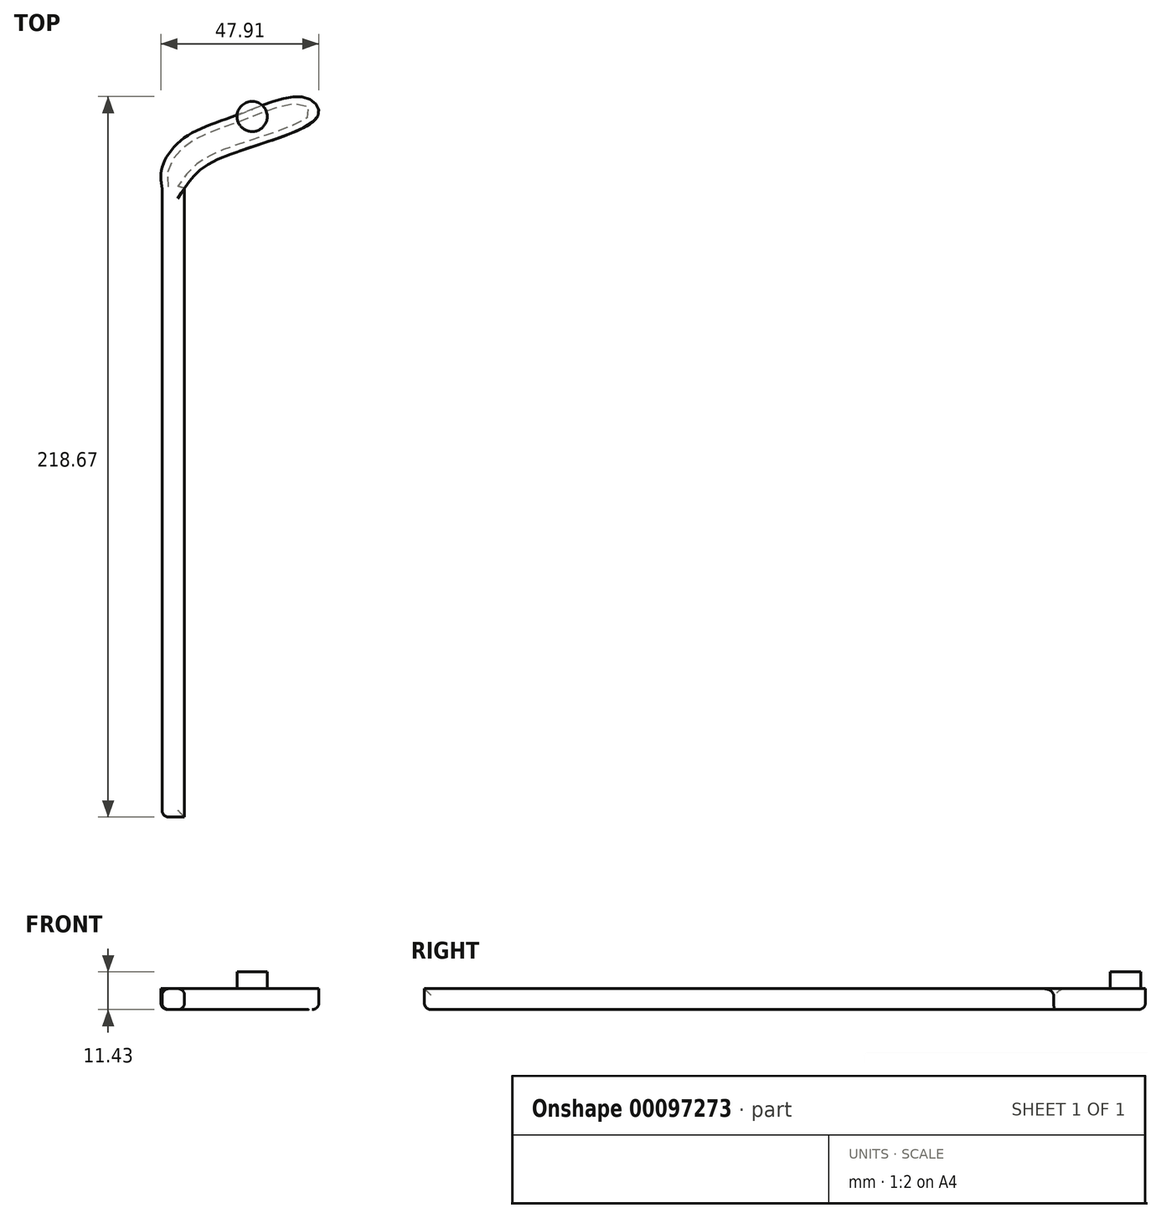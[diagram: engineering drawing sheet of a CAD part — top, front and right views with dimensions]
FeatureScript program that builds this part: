
annotation { "Feature Type Name" : "Feature", "Feature Type Description" : "" }
export const myFeature = defineFeature(function(context is Context, id is Id, definition is map)
    precondition{}
    {
        {
            var Q0;
            Q0=qCreatedBy(makeId("Top.planeOp"),FACE);
            var sketch = newSketch(context, id + "F0", { "sketchPlane" : qUnion([Q0])});
            skLineSegment(sketch, "E0.bottom", {"start": v(-18.72, 95.23) * mm, "end": v(-11.92, 95.23) * mm});
            skLineSegment(sketch, "E0.top", {"start": v(-18.72, -95.62) * mm, "end": v(-11.92, -95.62) * mm});
            skLineSegment(sketch, "E0.left", {"start": v(-18.72, 95.23) * mm, "end": v(-18.72, -95.62) * mm});
            skLineSegment(sketch, "E0.right", {"start": v(-11.92, 95.23) * mm, "end": v(-11.92, -95.62) * mm});
            skFitSpline(sketch, "E1", {"points": [v(-18.72, 95.23) * mm, v(-18.72, 101.6) * mm, v(-12.01, 110.52) * mm, v(5.67, 118.07) * mm, v(24.84, 122.7) * mm, v(28.45, 117) * mm, v(-2.58, 103.66) * mm, v(-11.92, 95.23) * mm], "startDerivative": vector(-9.74, 64.86) * mm, "endDerivative": vector(-42.36, -64.86) * mm});
            skSolve(sketch);
        }
        {
            var Q0;
            Q0=makeQuery(id+"F0.imprint","IMPRINT",FACE,{"disambiguationData":[TD([[makeQuery(id+"F0.imprint","IMPRINT",EDGE,{"derivedFrom":sQuery(id+"F0.wireOp",EDGE,"E0.bottom")}),1.0]])]});
            var Q1;
            Q1=makeQuery(id+"F0.imprint","IMPRINT",FACE,{"disambiguationData":[TD([[makeQuery(id+"F0.imprint","IMPRINT",EDGE,{"derivedFrom":sQuery(id+"F0.wireOp",EDGE,"E0.bottom")}),-1.0]])]});
            extrude(context, id + "F1", {"entities" : qUnion([Q0, Q1]), "depth" : 6.35 * mm});
        }
        {
            var Q0;
            Q0=makeQuery(id+"F1.opExtrude","CAP_EDGE",EDGE,{"disambiguationData":[OSD([sQuery(id+"F0.wireOp",EDGE,"E0.right")])],"isStart":true});
            var Q1;
            Q1=makeQuery(id+"F1.opExtrude","CAP_FACE",FACE,{"disambiguationData":[OSD([sQuery(id+"F0.wireOp",EDGE,"E0.top"),sQuery(id+"F0.wireOp",EDGE,"E0.left"),sQuery(id+"F0.wireOp",EDGE,"E0.right"),sQuery(id+"F0.wireOp",EDGE,"E1")])],"isStart":true});
            var Q2;
            Q2=makeQuery(id+"F1.opExtrude","SWEPT_FACE",FACE,{"disambiguationData":[OSD([sQuery(id+"F0.wireOp",EDGE,"E0.left")])]});
            var Q3;
            Q3=makeQuery(id+"F1.opExtrude","CAP_EDGE",EDGE,{"disambiguationData":[OSD([sQuery(id+"F0.wireOp",EDGE,"E0.left")])],"isStart":true});
            var Q4;
            Q4=makeQuery(id+"F1.opExtrude","CAP_EDGE",EDGE,{"disambiguationData":[OSD([sQuery(id+"F0.wireOp",EDGE,"E0.right")])],"isStart":false});
            fillet(context, id + "F2", {"entities" : qUnion([Q0, Q1, Q2, Q3, Q4]), "radius" : 2.03 * mm, "tangentPropagation" : true, "allowEdgeOverflow" : false});
        }
        {
            var Q0;
            Q0=makeQuery(id+"F1.opExtrude","CAP_FACE",FACE,{"disambiguationData":[OSD([sQuery(id+"F0.wireOp",EDGE,"E0.top"),sQuery(id+"F0.wireOp",EDGE,"E0.left"),sQuery(id+"F0.wireOp",EDGE,"E0.right"),sQuery(id+"F0.wireOp",EDGE,"E1")])],"isStart":false});
            var sketch = newSketch(context, id + "F3", { "sketchPlane" : qUnion([Q0])});
            skCircle(sketch, "E2", {"center": v(8.6, 117.02) * mm, "radius": 4.58 * mm});
            skSolve(sketch);
        }
        {
            var Q0;
            {var subQ0=sQuery(id+"F3.wireOp",EDGE,"E2");var subQ1=sQuery(id+"F0.wireOp",EDGE,"E1");var subQ2=makeQuery(id+"F2.opFillet","BLEND_EDGE",EDGE,{"blendedFrom":[makeQuery(id+"F1.opExtrude","CAP_EDGE",EDGE,{"disambiguationData":[OSD([subQ1])],"isStart":false}),makeQuery(id+"F1.opExtrude","CAP_FACE",FACE,{"disambiguationData":[OSD([sQuery(id+"F0.wireOp",EDGE,"E0.top"),sQuery(id+"F0.wireOp",EDGE,"E0.left"),sQuery(id+"F0.wireOp",EDGE,"E0.right"),subQ1])],"isStart":false})],"blendedInto":[makeQuery(id+"F1.opExtrude","CAP_FACE",FACE,{"disambiguationData":[OSD([sQuery(id+"F0.wireOp",EDGE,"E0.top"),sQuery(id+"F0.wireOp",EDGE,"E0.left"),sQuery(id+"F0.wireOp",EDGE,"E0.right"),subQ1])],"isStart":false})]});var subQ3=makeQuery(id+"F3.imprint","INTERSECT",VERTEX,{"disambiguationData":[OD(0.0)],"derivedFrom":[subQ2,subQ0]});Q0=makeQuery(id+"F3.imprint","IMPRINT",FACE,{"disambiguationData":[TD([[makeQuery(id+"F3.imprint","IMPRINT",EDGE,{"disambiguationData":[TD([[subQ3,1.0]])],"derivedFrom":subQ0}),1.0]])]});}
            var Q1;
            {var subQ0=sQuery(id+"F3.wireOp",EDGE,"E2");var subQ1=sQuery(id+"F0.wireOp",EDGE,"E1");var subQ2=makeQuery(id+"F2.opFillet","BLEND_EDGE",EDGE,{"blendedFrom":[makeQuery(id+"F1.opExtrude","CAP_EDGE",EDGE,{"disambiguationData":[OSD([subQ1])],"isStart":false}),makeQuery(id+"F1.opExtrude","CAP_FACE",FACE,{"disambiguationData":[OSD([sQuery(id+"F0.wireOp",EDGE,"E0.top"),sQuery(id+"F0.wireOp",EDGE,"E0.left"),sQuery(id+"F0.wireOp",EDGE,"E0.right"),subQ1])],"isStart":false})],"blendedInto":[makeQuery(id+"F1.opExtrude","CAP_FACE",FACE,{"disambiguationData":[OSD([sQuery(id+"F0.wireOp",EDGE,"E0.top"),sQuery(id+"F0.wireOp",EDGE,"E0.left"),sQuery(id+"F0.wireOp",EDGE,"E0.right"),subQ1])],"isStart":false})]});var subQ3=makeQuery(id+"F3.imprint","INTERSECT",VERTEX,{"disambiguationData":[OD(0.0)],"derivedFrom":[subQ2,subQ0]});Q1=makeQuery(id+"F3.imprint","IMPRINT",FACE,{"disambiguationData":[TD([[makeQuery(id+"F3.imprint","IMPRINT",EDGE,{"disambiguationData":[TD([[subQ3,-1.0]])],"derivedFrom":subQ0}),1.0]])]});}
            extrude(context, id + "F4", {"entities" : qUnion([Q0, Q1]), "operationType" : NewBodyOperationType.ADD, "depth" : 5.08 * mm});
        }
    });
